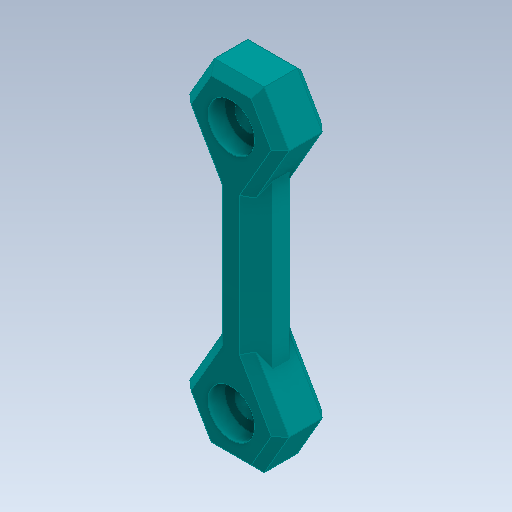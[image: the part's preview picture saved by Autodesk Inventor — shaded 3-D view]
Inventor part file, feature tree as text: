
AUTODESK INVENTOR PART (.ipt)
format: ipt  version: 2020 (Build 240168000, 168)  size: 197,120 bytes
history: native  units: in
note: dims shown in document units (in); Inventor stores cm internally (conversion verified against a paired STEP export)
features: extrude x2, chamfer x2, sketch x2, mirror x1, projected_geometry x1
ambient origin geometry x8: Origin, YZ Plane, XZ Plane, XY Plane, X Axis, Y Axis, Z Axis, Center Point
bodies: Solid1 (feature_tree)
feature tree (8):
  extrude  "Extrusion1"  Depth=0.2362in
  extrude  "Extrusion2"  Depth=0.0787in
  chamfer  "Chamfer1"  Distance=0.2362in
  chamfer  "Chamfer2"  Distance=1.1811in
  mirror  "Mirror1"
  sketch  "Sketch1"  dims[d0=0.122in d1=0.2362in]
  sketch  "Sketch2"  dims[d2=1.1811in d3=0.122in d4=0.2362in d5=1.1811in d6=0.1181in d7=0.2362in d8=0.2362in d9=0.1181in d10=0.0in d11=0.2205in d12=0.2205in d13=0.0787in d14=0.0in d15=0.0787in d16=0.0787in d17=45.0deg d18=0.0394in d19=0.0787in d20=45.0deg]
  projected_geometry  "Projected Loop1"
